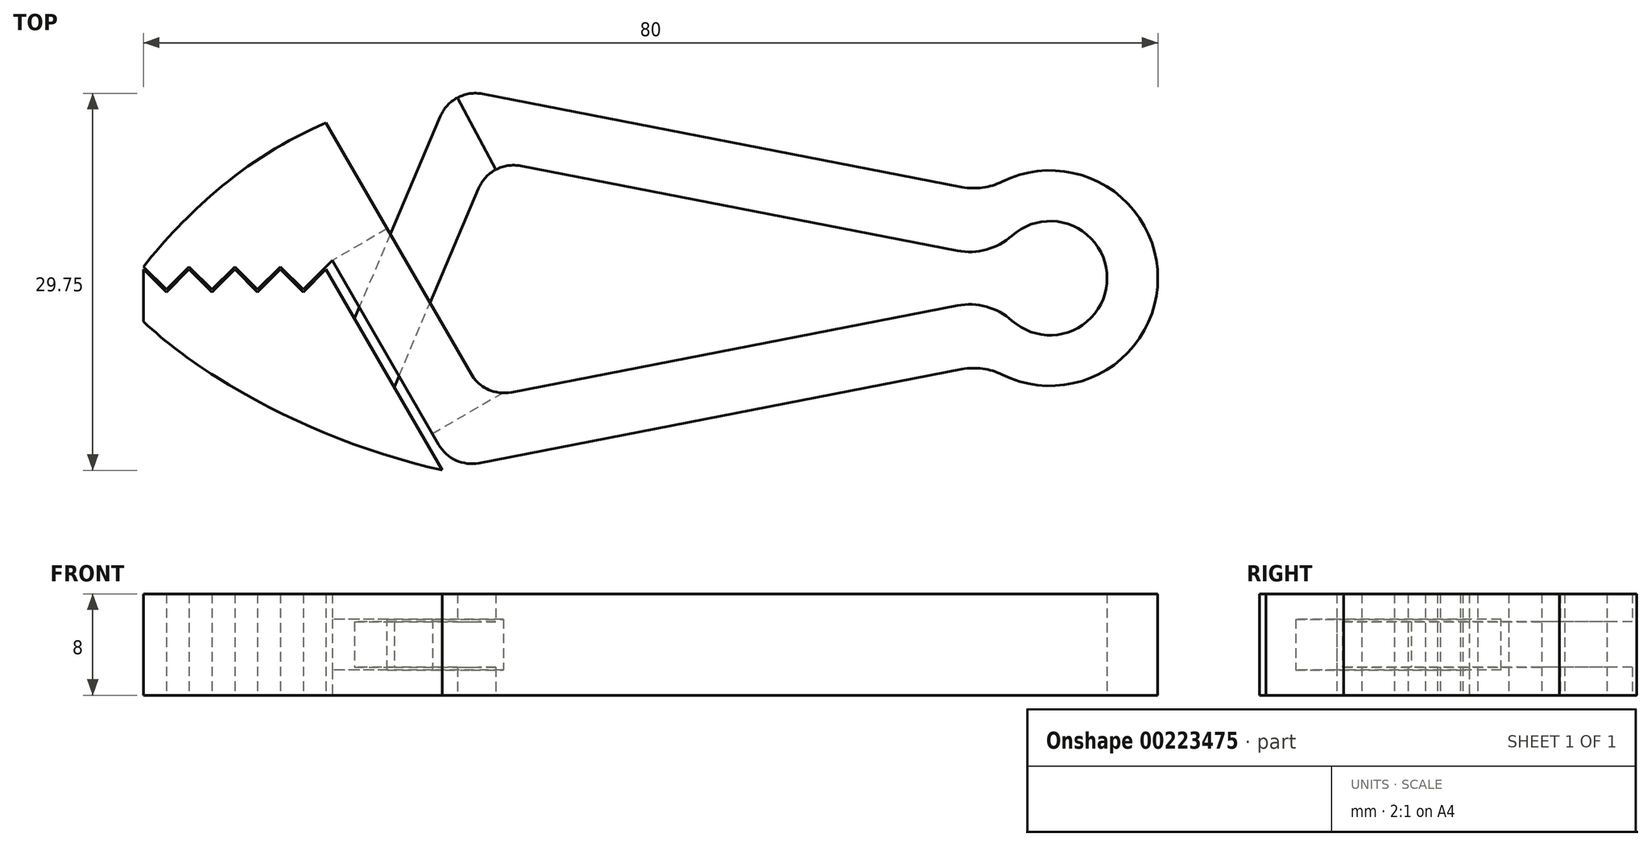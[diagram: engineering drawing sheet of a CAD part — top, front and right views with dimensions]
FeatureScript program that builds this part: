
annotation { "Feature Type Name" : "Feature", "Feature Type Description" : "" }
export const myFeature = defineFeature(function(context is Context, id is Id, definition is map)
    precondition{}
    {
        {
            var Q0;
            Q0=qCreatedBy(makeId("Top.planeOp"),FACE);
            var sketch = newSketch(context, id + "F0", { "sketchPlane" : qUnion([Q0])});
            skArc(sketch, "E0", {"start": v(43.36, -7.62) * mm, "mid": v(55.64, 0) * mm, "end": v(43.36, 7.62) * mm});
            skLineSegment(sketch, "E1", {"start": v(-24.36, 0.9) * mm, "end": v(-22.56, -0.9) * mm});
            skLineSegment(sketch, "E2", {"start": v(-22.56, -0.9) * mm, "end": v(-20.76, 0.9) * mm});
            skLineSegment(sketch, "E3", {"start": v(-20.76, 0.9) * mm, "end": v(-18.96, -0.9) * mm});
            skLineSegment(sketch, "E4", {"start": v(-18.96, -0.9) * mm, "end": v(-17.16, 0.9) * mm});
            skLineSegment(sketch, "E5", {"start": v(-17.16, 0.9) * mm, "end": v(-15.36, -0.9) * mm});
            skLineSegment(sketch, "E6", {"start": v(-15.36, -0.9) * mm, "end": v(-13.56, 0.9) * mm});
            skLineSegment(sketch, "E7", {"start": v(-13.56, 0.9) * mm, "end": v(-11.76, -0.9) * mm});
            skLineSegment(sketch, "E8", {"start": v(-11.76, -0.9) * mm, "end": v(-9.96, 0.9) * mm});
            skLineSegment(sketch, "E9", {"start": v(-9.96, 0.9) * mm, "end": v(-9.47, 1.4) * mm});
            skLineSegment(sketch, "E10", {"start": v(-9.47, 1.4) * mm, "end": v(-1.07, -13.15) * mm});
            skLineSegment(sketch, "E11", {"start": v(-0.8, -15.16) * mm, "end": v(-9.96, 0.7) * mm});
            skLineSegment(sketch, "E12", {"start": v(-9.96, 0.7) * mm, "end": v(-11.76, -1.1) * mm});
            skLineSegment(sketch, "E13", {"start": v(-11.76, -1.1) * mm, "end": v(-13.56, 0.7) * mm});
            skLineSegment(sketch, "E14", {"start": v(-13.56, 0.7) * mm, "end": v(-15.36, -1.1) * mm});
            skLineSegment(sketch, "E15", {"start": v(-15.36, -1.1) * mm, "end": v(-17.16, 0.7) * mm});
            skLineSegment(sketch, "E16", {"start": v(-17.16, 0.7) * mm, "end": v(-18.96, -1.1) * mm});
            skLineSegment(sketch, "E17", {"start": v(-18.96, -1.1) * mm, "end": v(-20.76, 0.7) * mm});
            skLineSegment(sketch, "E18", {"start": v(-20.76, 0.7) * mm, "end": v(-22.56, -1.1) * mm});
            skLineSegment(sketch, "E19", {"start": v(-22.56, -1.1) * mm, "end": v(-24.36, 0.7) * mm});
            skLineSegment(sketch, "E20", {"start": v(-24.36, 0.7) * mm, "end": v(-24.36, -3.44) * mm});
            skPoint(sketch, "E21", {"position": v(-23.46, 0) * mm});
            skLineSegment(sketch, "E22", {"start": v(-9.96, 12.26) * mm, "end": v(1.48, -7.56) * mm});
            skLineSegment(sketch, "E23", {"start": v(40.19, -7.19) * mm, "end": v(2.1, -14.6) * mm});
            skLineSegment(sketch, "E24", {"start": v(0, -15) * mm, "end": v(-0.8, -15.16) * mm, "construction": true});
            skArc(sketch, "E25", {"start": v(44.13, -3.35) * mm, "mid": v(51.64, 0) * mm, "end": v(44.13, 3.35) * mm});
            skLineSegment(sketch, "E26", {"start": v(4.65, -9) * mm, "end": v(39.84, -2.16) * mm});
            skArc(sketch, "E27", {"start": v(-24.36, -3.44) * mm, "mid": v(-21.6, -5.74) * mm, "end": v(-18.66, -7.78) * mm});
            skArc(sketch, "E28", {"start": v(-18.66, -7.78) * mm, "mid": v(-10.04, -12.22) * mm, "end": v(-0.8, -15.16) * mm});
            skArc(sketch, "E29", {"start": v(-18.66, 6.84) * mm, "mid": v(-21.65, 4.01) * mm, "end": v(-24.36, 0.9) * mm});
            skArc(sketch, "E30", {"start": v(-9.96, 12.26) * mm, "mid": v(-14.51, 9.88) * mm, "end": v(-18.66, 6.84) * mm});
            skPoint(sketch, "E31", {"position": v(-9.96, -12.26) * mm});
            skLineSegment(sketch, "E32", {"start": v(-9.96, 12.26) * mm, "end": v(-9.96, -12.26) * mm, "construction": true});
            skPoint(sketch, "E33", {"position": v(-9.96, 0) * mm});
            skLineSegment(sketch, "E34", {"start": v(-0.95, 12.76) * mm, "end": v(-3.91, 5.78) * mm});
            skLineSegment(sketch, "E35", {"start": v(0.69, 3.83) * mm, "end": v(2.07, 7.08) * mm});
            skLineSegment(sketch, "E36", {"start": v(5.4, 8.86) * mm, "end": v(39.84, 2.16) * mm});
            skLineSegment(sketch, "E37", {"start": v(2.38, 14.54) * mm, "end": v(40.19, 7.19) * mm});
            skLineSegment(sketch, "E38", {"start": v(0, 15) * mm, "end": v(0, -15) * mm, "construction": true});
            skPoint(sketch, "E39", {"position": v(0, 0) * mm});
            skPoint(sketch, "E40.visualSharp", {"position": v(3.02, 9.32) * mm});
            skArc(sketch, "E40.filletArc", {"start": v(5.4, 8.86) * mm, "mid": v(3.42, 8.56) * mm, "end": v(2.07, 7.08) * mm});
            skPoint(sketch, "E41.visualSharp", {"position": v(2.55, -9.41) * mm});
            skArc(sketch, "E41.filletArc", {"start": v(1.48, -7.56) * mm, "mid": v(2.83, -8.79) * mm, "end": v(4.65, -9) * mm});
            skPoint(sketch, "E42.visualSharp", {"position": v(0, 15) * mm});
            skArc(sketch, "E42.filletArc", {"start": v(2.38, 14.54) * mm, "mid": v(0.4, 14.24) * mm, "end": v(-0.95, 12.76) * mm});
            skPoint(sketch, "E43.visualSharp", {"position": v(0, -15) * mm});
            skArc(sketch, "E43.filletArc", {"start": v(-1.07, -13.15) * mm, "mid": v(0.28, -14.38) * mm, "end": v(2.1, -14.6) * mm});
            skPoint(sketch, "E44.visualSharp", {"position": v(42.92, -1.56) * mm});
            skArc(sketch, "E44.filletArc", {"start": v(44.13, -3.35) * mm, "mid": v(42.12, -2.25) * mm, "end": v(39.84, -2.16) * mm});
            skPoint(sketch, "E45.visualSharp", {"position": v(42.92, 1.56) * mm});
            skArc(sketch, "E45.filletArc", {"start": v(39.84, 2.16) * mm, "mid": v(42.12, 2.25) * mm, "end": v(44.13, 3.35) * mm});
            skPoint(sketch, "E46.visualSharp", {"position": v(42.07, 6.82) * mm});
            skArc(sketch, "E46.filletArc", {"start": v(40.19, 7.19) * mm, "mid": v(41.81, 7.14) * mm, "end": v(43.36, 7.62) * mm});
            skPoint(sketch, "E47.visualSharp", {"position": v(42.07, -6.82) * mm});
            skArc(sketch, "E47.filletArc", {"start": v(43.36, -7.62) * mm, "mid": v(41.81, -7.14) * mm, "end": v(40.19, -7.19) * mm});
            skLineSegment(sketch, "E48", {"start": v(-18.66, -7.78) * mm, "end": v(-18.66, 6.84) * mm, "construction": true});
            skLineSegment(sketch, "E49", {"start": v(-3.91, 5.78) * mm, "end": v(0.69, 3.83) * mm});
            skSolve(sketch);
        }
        {
            var Q0;
            Q0 = qSketchRegion(id + "F0", true);
            extrude(context, id + "F1", {"entities" : qUnion([Q0]), "endBound" : BoundingType.SYMMETRIC, "depth" : 8 * mm});
        }
        {
            var Q0;
            Q0=makeQuery(id+"F1.opExtrude","SWEPT_FACE",FACE,{"disambiguationData":[OSD([sQuery(id+"F0.wireOp",EDGE,"E10")])]});
            var sketch = newSketch(context, id + "F2", { "sketchPlane" : qUnion([Q0])});
            skLineSegment(sketch, "E50.bottom", {"start": v(9.85, 2) * mm, "end": v(-5.94, 2) * mm});
            skLineSegment(sketch, "E50.top", {"start": v(9.85, -2) * mm, "end": v(-5.94, -2) * mm});
            skLineSegment(sketch, "E50.left", {"start": v(9.85, 2) * mm, "end": v(9.85, -2) * mm});
            skLineSegment(sketch, "E50.right", {"start": v(-5.94, 2) * mm, "end": v(-5.94, -2) * mm});
            skPoint(sketch, "E50.middle", {"position": v(1.95, 0) * mm});
            skSolve(sketch);
        }
        {
            var Q0;
            Q0 = qSketchRegion(id + "F2", true);
            var Q1;
            Q1=makeQuery(id+"F1.opExtrude","SWEPT_FACE",FACE,{"disambiguationData":[OSD([sQuery(id+"F0.wireOp",EDGE,"N29QUHej-50zl-2zG0-MLSK-mSxDUbjKBQph")])]});
            extrude(context, id + "F3", {"entities" : qUnion([Q0]), "operationType" : NewBodyOperationType.REMOVE, "oppositeDirection" : true, "endBoundEntityFace" : qUnion([Q1]), "depth" : 7 * mm});
        }
        {
            var Q0;
            Q0=makeQuery(id+"F1.opExtrude","CAP_EDGE",EDGE,{"disambiguationData":[OSD([sQuery(id+"F0.wireOp",EDGE,"E42.filletArc")])],"isStart":true});
            cPoint(context, id + "F4", {"entities" : qUnion([Q0]), "parameter" : 0.5});
        }
        {
            var Q0;
            Q0=makeQuery(id+"F1.opExtrude","CAP_EDGE",EDGE,{"disambiguationData":[OSD([sQuery(id+"F0.wireOp",EDGE,"E42.filletArc")])],"isStart":true});
            var Q1;
            Q1 = qCreatedBy(id + "F4" ,VERTEX);
            cPlane(context, id + "F5", {"entities" : qUnion([Q0, Q1]), "cplaneType" : CPlaneType.CURVE_POINT, "offset" : 25 * mm, "width" : 150 * mm, "height" : 150 * mm});
        }
        {
            var Q0;
            Q0=qCreatedBy(id+"F5.planeOp",FACE);
            var sketch = newSketch(context, id + "F6", { "sketchPlane" : qUnion([Q0])});
            skLineSegment(sketch, "E51", {"start": v(-20.71, 0) * mm, "end": v(-2.02, 0) * mm, "construction": true});
            skLineSegment(sketch, "E52.bottom", {"start": v(-16.5, -4) * mm, "end": v(-3.05, -4) * mm});
            skLineSegment(sketch, "E52.top", {"start": v(-16.5, -1.8) * mm, "end": v(-3.05, -1.8) * mm});
            skLineSegment(sketch, "E52.left", {"start": v(-16.5, -4) * mm, "end": v(-16.5, -1.8) * mm});
            skLineSegment(sketch, "E52.right", {"start": v(-3.05, -4) * mm, "end": v(-3.05, -1.8) * mm});
            skLineSegment(sketch, "E53.bottom", {"start": v(-16.5, 1.8) * mm, "end": v(-3.05, 1.8) * mm});
            skLineSegment(sketch, "E53.top", {"start": v(-16.5, 4) * mm, "end": v(-3.05, 4) * mm});
            skLineSegment(sketch, "E53.left", {"start": v(-16.5, 1.8) * mm, "end": v(-16.5, 4) * mm});
            skLineSegment(sketch, "E53.right", {"start": v(-3.05, 1.8) * mm, "end": v(-3.05, 4) * mm});
            skLineSegment(sketch, "E54", {"start": v(-16.5, -1.8) * mm, "end": v(-16.5, 0) * mm, "construction": true});
            skLineSegment(sketch, "E55", {"start": v(-16.5, 0) * mm, "end": v(-16.5, 1.8) * mm, "construction": true});
            skSolve(sketch);
        }
        {
            var Q0;
            Q0 = qSketchRegion(id + "F6", true);
            extrude(context, id + "F7", {"entities" : qUnion([Q0]), "operationType" : NewBodyOperationType.REMOVE, "depth" : 8 * mm});
        }
        {
            var Q0;
            Q0=makeQuery(id+"F1.opExtrude","SWEPT_FACE",FACE,{"disambiguationData":[OSD([sQuery(id+"F0.wireOp",EDGE,"E49")])]});
            var Q1;
            Q1=makeQuery(id+"F1.opExtrude","SWEPT_FACE",FACE,{"disambiguationData":[OSD([sQuery(id+"F0.wireOp",EDGE,"E11")])]});
            extrude(context, id + "F8", {"entities" : qUnion([Q0]), "operationType" : NewBodyOperationType.ADD, "endBound" : BoundingType.UP_TO_SURFACE, "endBoundEntityFace" : qUnion([Q1]), "depth" : 25 * mm});
        }
    });
